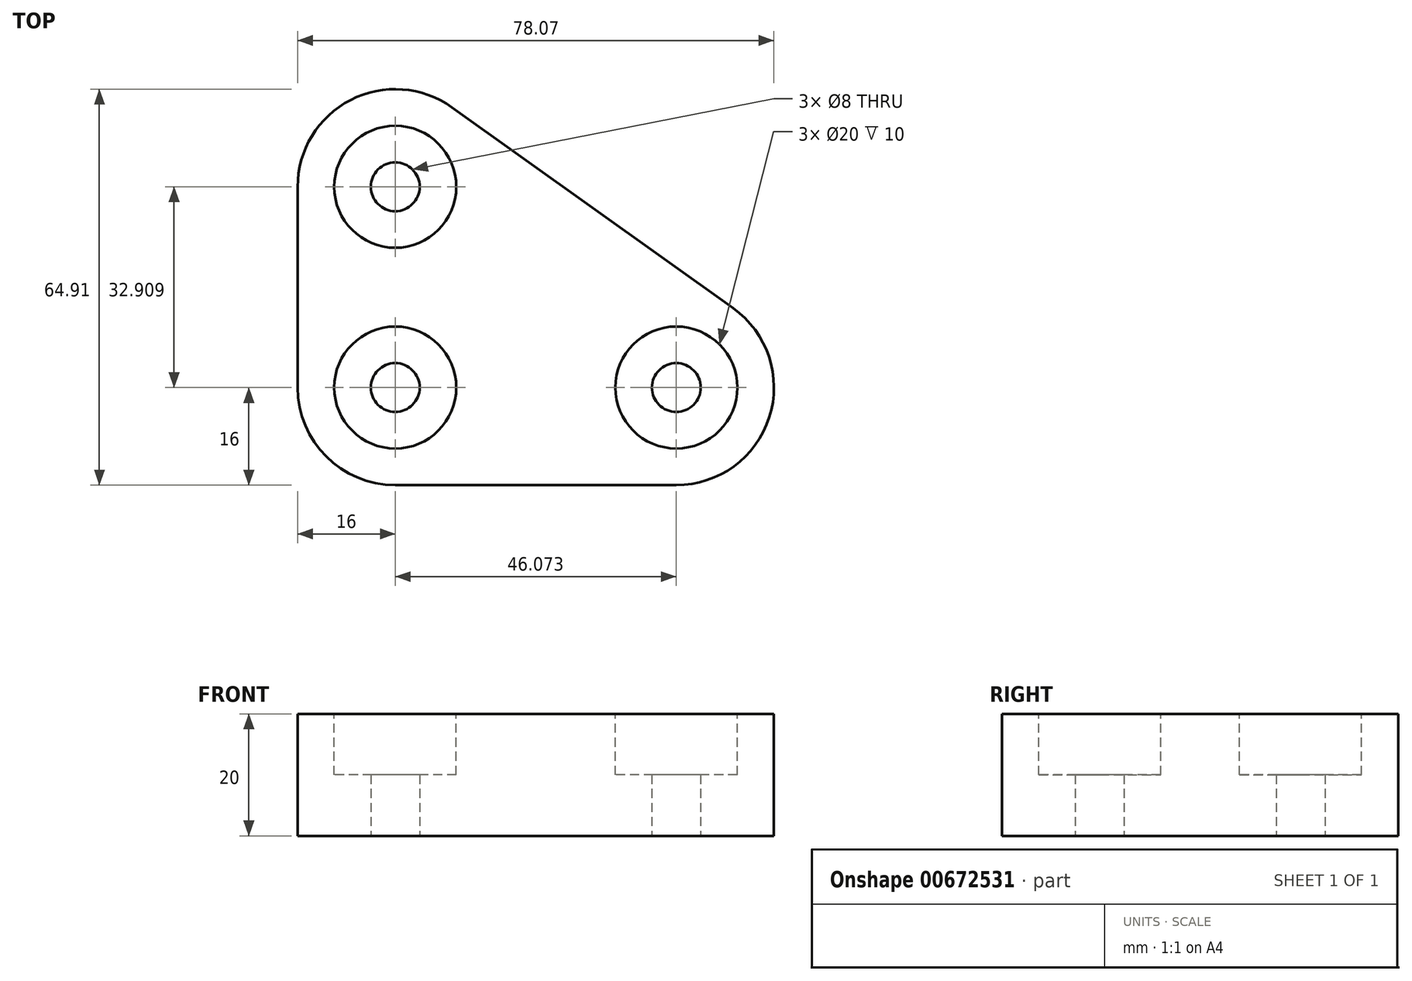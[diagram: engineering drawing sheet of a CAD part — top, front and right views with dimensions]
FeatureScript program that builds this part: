
annotation { "Feature Type Name" : "Feature", "Feature Type Description" : "" }
export const myFeature = defineFeature(function(context is Context, id is Id, definition is map)
    precondition{}
    {
        {
            var Q0;
            Q0=qCreatedBy(makeId("Top.planeOp"),FACE);
            var sketch = newSketch(context, id + "F0", { "sketchPlane" : qUnion([Q0])});
            skLineSegment(sketch, "E0.bottom", {"start": v(16, 0) * mm, "end": v(62.07, 0) * mm});
            skLineSegment(sketch, "E0.left", {"start": v(0, 16) * mm, "end": v(0, 48.9) * mm});
            skLineSegment(sketch, "E1", {"start": v(25.3, 61.93) * mm, "end": v(71.37, 29.02) * mm});
            skPoint(sketch, "E2.visualSharp", {"position": v(0, 80) * mm});
            skArc(sketch, "E2.filletArc", {"start": v(25.3, 61.93) * mm, "mid": v(8.68, 63.14) * mm, "end": v(0, 48.9) * mm});
            skPoint(sketch, "E3.visualSharp", {"position": v(112, 0) * mm});
            skArc(sketch, "E3.filletArc", {"start": v(62.07, 0) * mm, "mid": v(77.3, 11.12) * mm, "end": v(71.37, 29.02) * mm});
            skPoint(sketch, "E4.visualSharp", {"position": v(0, 0) * mm});
            skArc(sketch, "E4.filletArc", {"start": v(0, 16) * mm, "mid": v(4.69, 4.69) * mm, "end": v(16, 0) * mm});
            skCircle(sketch, "E5", {"center": v(16, 48.9) * mm, "radius": 10 * mm});
            skCircle(sketch, "E6", {"center": v(62.07, 16) * mm, "radius": 10 * mm});
            skCircle(sketch, "E7", {"center": v(16, 16) * mm, "radius": 10 * mm});
            skCircle(sketch, "E8", {"center": v(16, 48.9) * mm, "radius": 4 * mm});
            skCircle(sketch, "E9", {"center": v(16, 16) * mm, "radius": 4 * mm});
            skCircle(sketch, "E10", {"center": v(62.07, 16) * mm, "radius": 4 * mm});
            skSolve(sketch);
        }
        {
            var Q0;
            Q0=makeQuery(id+"F0.imprint","IMPRINT",FACE,{"disambiguationData":[TD([[makeQuery(id+"F0.imprint","IMPRINT",EDGE,{"derivedFrom":sQuery(id+"F0.wireOp",EDGE,"E0.bottom")}),1.0]])]});
            var Q1;
            Q1=makeQuery(id+"F0.imprint","IMPRINT",FACE,{"disambiguationData":[TD([[makeQuery(id+"F0.imprint","IMPRINT",EDGE,{"derivedFrom":sQuery(id+"F0.wireOp",EDGE,"E5")}),1.0]])]});
            var Q2;
            Q2=makeQuery(id+"F0.imprint","IMPRINT",FACE,{"disambiguationData":[TD([[makeQuery(id+"F0.imprint","IMPRINT",EDGE,{"derivedFrom":sQuery(id+"F0.wireOp",EDGE,"E6")}),1.0]])]});
            var Q3;
            Q3=makeQuery(id+"F0.imprint","IMPRINT",FACE,{"disambiguationData":[TD([[makeQuery(id+"F0.imprint","IMPRINT",EDGE,{"derivedFrom":sQuery(id+"F0.wireOp",EDGE,"E7")}),1.0]])]});
            extrude(context, id + "F1", {"entities" : qUnion([Q0, Q1, Q2, Q3]), "depth" : 20 * mm, "offsetDistance" : 25 * mm});
        }
        {
            var Q0;
            Q0=makeQuery(id+"F1.opExtrude","CAP_FACE",FACE,{"disambiguationData":[OSD([sQuery(id+"F0.wireOp",EDGE,"E0.bottom"),sQuery(id+"F0.wireOp",EDGE,"E0.left"),sQuery(id+"F0.wireOp",EDGE,"E1"),sQuery(id+"F0.wireOp",EDGE,"E2.filletArc"),sQuery(id+"F0.wireOp",EDGE,"E3.filletArc"),sQuery(id+"F0.wireOp",EDGE,"E4.filletArc"),sQuery(id+"F0.wireOp",EDGE,"E8"),sQuery(id+"F0.wireOp",EDGE,"E9"),sQuery(id+"F0.wireOp",EDGE,"E10")])],"isStart":false});
            var sketch = newSketch(context, id + "F2", { "sketchPlane" : qUnion([Q0])});
            skCircle(sketch, "E11", {"center": v(16, 48.9) * mm, "radius": 10 * mm});
            skCircle(sketch, "E12", {"center": v(62.07, 16) * mm, "radius": 10 * mm});
            skCircle(sketch, "E13", {"center": v(16, 16) * mm, "radius": 10 * mm});
            skSolve(sketch);
        }
        {
            var Q0;
            Q0=makeQuery(id+"F2.imprint","IMPRINT",FACE,{"disambiguationData":[TD([[makeQuery(id+"F2.imprint","IMPRINT",EDGE,{"derivedFrom":sQuery(id+"F2.wireOp",EDGE,"E11")}),1.0]])]});
            var Q1;
            Q1=makeQuery(id+"F2.imprint","IMPRINT",FACE,{"disambiguationData":[TD([[makeQuery(id+"F2.imprint","IMPRINT",EDGE,{"derivedFrom":sQuery(id+"F2.wireOp",EDGE,"E13")}),1.0]])]});
            var Q2;
            Q2=makeQuery(id+"F2.imprint","IMPRINT",FACE,{"disambiguationData":[TD([[makeQuery(id+"F2.imprint","IMPRINT",EDGE,{"derivedFrom":sQuery(id+"F2.wireOp",EDGE,"E12")}),1.0]])]});
            extrude(context, id + "F3", {"entities" : qUnion([Q0, Q1, Q2]), "operationType" : NewBodyOperationType.REMOVE, "oppositeDirection" : true, "depth" : 10 * mm, "offsetDistance" : 25 * mm});
        }
    });
